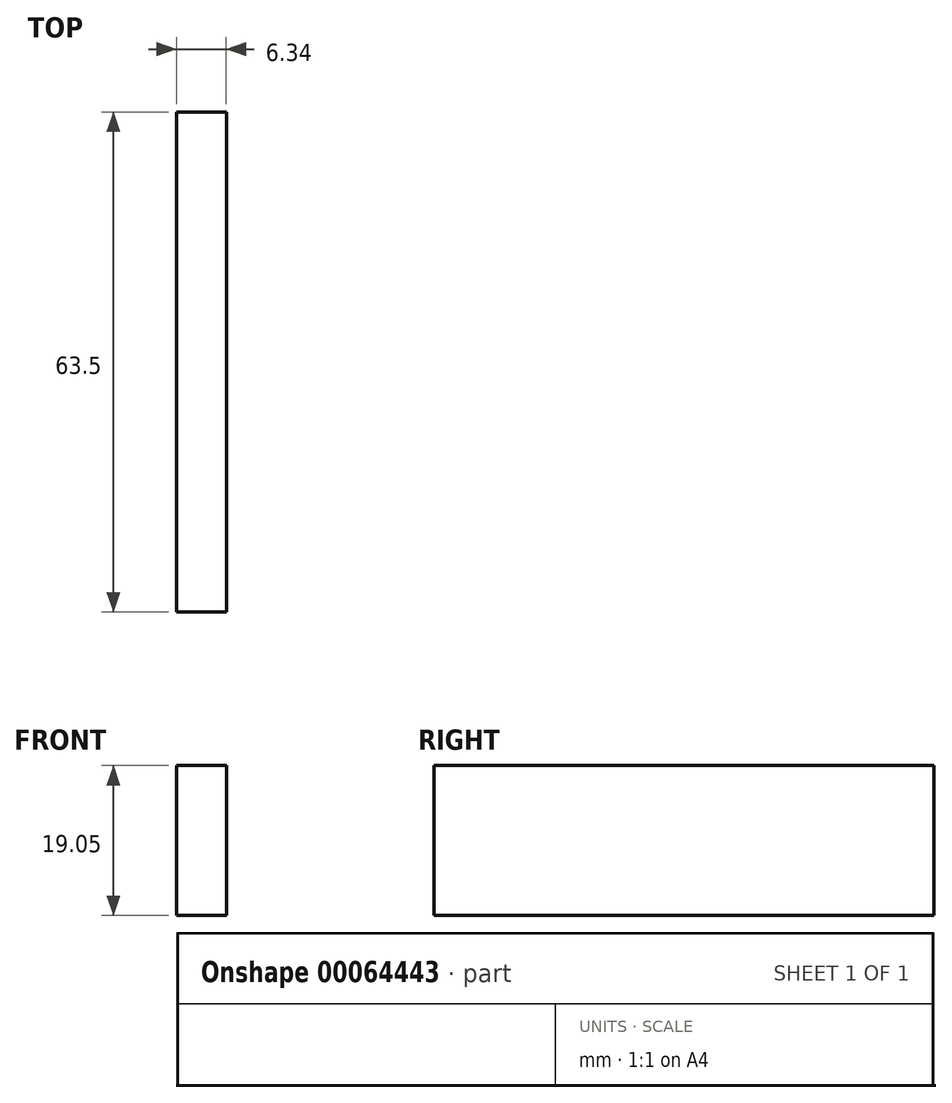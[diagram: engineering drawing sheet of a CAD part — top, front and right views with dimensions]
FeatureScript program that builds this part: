
annotation { "Feature Type Name" : "Feature", "Feature Type Description" : "" }
export const myFeature = defineFeature(function(context is Context, id is Id, definition is map)
    precondition{}
    {
        {
            var Q0;
            Q0=qCreatedBy(makeId("Top.planeOp"),FACE);
            var sketch = newSketch(context, id + "F0", { "sketchPlane" : qUnion([Q0])});
            skLineSegment(sketch, "E0.rect.bottom", {"start": v(-3.17, 31.75) * mm, "end": v(3.18, 31.75) * mm});
            skLineSegment(sketch, "E0.rect.top", {"start": v(-3.18, -31.75) * mm, "end": v(3.17, -31.75) * mm});
            skLineSegment(sketch, "E0.rect.left", {"start": v(-3.17, 31.75) * mm, "end": v(-3.18, -31.75) * mm});
            skLineSegment(sketch, "E0.rect.right", {"start": v(3.18, 31.75) * mm, "end": v(3.17, -31.75) * mm});
            skPoint(sketch, "E0.rect.middle", {"position": v(0, 0) * mm});
            skSolve(sketch);
        }
        {
            var Q0;
            Q0 = qSketchRegion(id + "F0", true);
            extrude(context, id + "F1", {"entities" : qUnion([Q0]), "depth" : 19.05 * mm});
        }
    });
